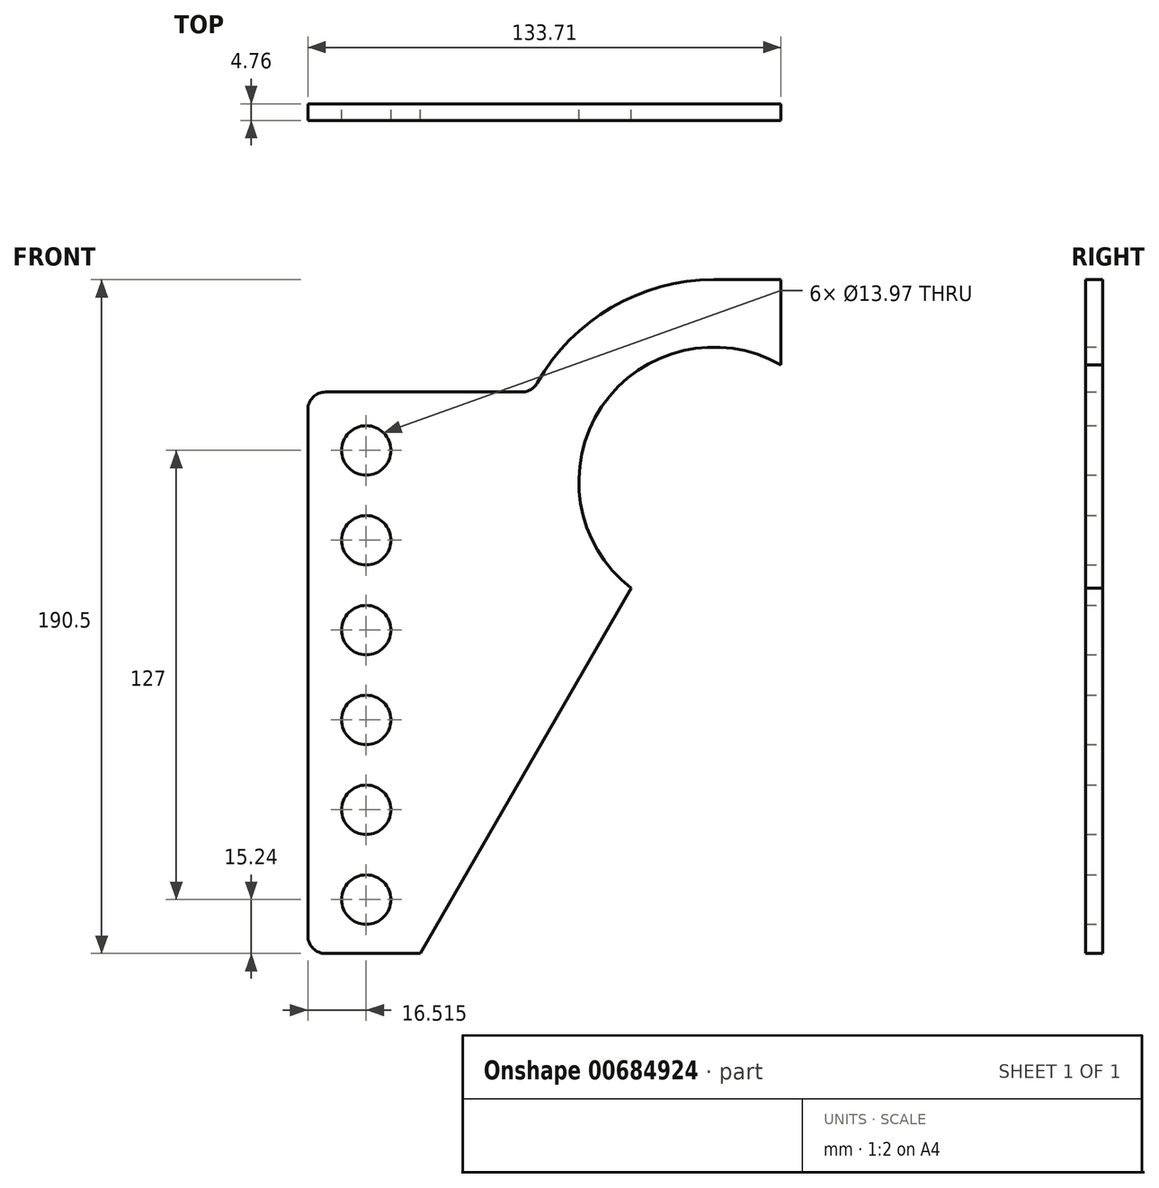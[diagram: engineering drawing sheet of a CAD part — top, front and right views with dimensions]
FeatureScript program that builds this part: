
annotation { "Feature Type Name" : "Feature", "Feature Type Description" : "" }
export const myFeature = defineFeature(function(context is Context, id is Id, definition is map)
    precondition{}
    {
        {
            var Q0;
            Q0=qCreatedBy(makeId("Front.planeOp"),FACE);
            var sketch = newSketch(context, id + "F0", { "sketchPlane" : qUnion([Q0])});
            skCircle(sketch, "E0", {"center": v(0, 0) * mm, "radius": 38.1 * mm, "construction": true});
            skCircle(sketch, "E1", {"center": v(0, 0) * mm, "radius": 57.15 * mm, "construction": true});
            skLineSegment(sketch, "E2", {"start": v(-75.8, 0) * mm, "end": v(76.4, 0) * mm, "construction": true});
            skLineSegment(sketch, "E3", {"start": v(0, 67.23) * mm, "end": v(0, -64.52) * mm, "construction": true});
            skLineSegment(sketch, "E4", {"start": v(57.15, 67.23) * mm, "end": v(57.15, -71.44) * mm, "construction": true});
            skLineSegment(sketch, "E5", {"start": v(0, 57.15) * mm, "end": v(19, 57.15) * mm});
            skLineSegment(sketch, "E6", {"start": v(19, 57.15) * mm, "end": v(19, 33.02) * mm});
            skLineSegment(sketch, "E7", {"start": v(-51.2, 25.4) * mm, "end": v(-114.7, 25.4) * mm});
            skLineSegment(sketch, "E8", {"start": v(-114.7, 25.4) * mm, "end": v(-114.7, -133.35) * mm});
            skLineSegment(sketch, "E9", {"start": v(-114.7, -133.35) * mm, "end": v(-82.95, -133.35) * mm});
            skLineSegment(sketch, "E10", {"start": v(-82.95, -133.35) * mm, "end": v(-23.34, -30.11) * mm});
            skLineSegment(sketch, "E11", {"start": v(-98.19, 66.97) * mm, "end": v(-98.19, -153.8) * mm, "construction": true});
            skCircle(sketch, "E12", {"center": v(-98.19, 8.89) * mm, "radius": 6.99 * mm});
            skCircle(sketch, "E13", {"center": v(-98.19, -16.51) * mm, "radius": 6.99 * mm});
            skCircle(sketch, "E14", {"center": v(-98.19, -41.91) * mm, "radius": 6.99 * mm});
            skCircle(sketch, "E15", {"center": v(-98.19, -67.31) * mm, "radius": 6.99 * mm});
            skCircle(sketch, "E16", {"center": v(-98.19, -92.71) * mm, "radius": 6.99 * mm});
            skCircle(sketch, "E17", {"center": v(-98.19, -118.11) * mm, "radius": 6.99 * mm});
            skArc(sketch, "E18", {"start": v(19, 33.02) * mm, "mid": v(-31.64, 21.22) * mm, "end": v(-23.34, -30.11) * mm});
            skArc(sketch, "E19", {"start": v(0, 57.15) * mm, "mid": v(-30.12, 48.57) * mm, "end": v(-51.2, 25.4) * mm});
            skSolve(sketch);
        }
        {
            var Q0;
            Q0=qSketchRegion(id+"F0",true);
            extrude(context, id + "F1", {"entities" : qUnion([Q0]), "depth" : 4.76 * mm, "offsetDistance" : 25.4 * mm});
        }
        {
            var Q0;
            Q0=makeQuery(id+"F1.opExtrude","SWEPT_EDGE",EDGE,{"disambiguationData":[OSD([sQuery(id+"F0.wireOp",EDGE,"E7"),sQuery(id+"F0.wireOp",EDGE,"E19")])]});
            var Q1;
            Q1=makeQuery(id+"F1.opExtrude","SWEPT_EDGE",EDGE,{"disambiguationData":[OSD([sQuery(id+"F0.wireOp",EDGE,"E8"),sQuery(id+"F0.wireOp",EDGE,"E9")])]});
            var Q2;
            Q2=makeQuery(id+"F1.opExtrude","SWEPT_EDGE",EDGE,{"disambiguationData":[OSD([sQuery(id+"F0.wireOp",EDGE,"E7"),sQuery(id+"F0.wireOp",EDGE,"E8")])]});
            fillet(context, id + "F2", {"entities" : qUnion([Q0, Q1, Q2]), "radius" : 5.08 * mm, "tangentPropagation" : true, "allowEdgeOverflow" : false});
        }
    });
